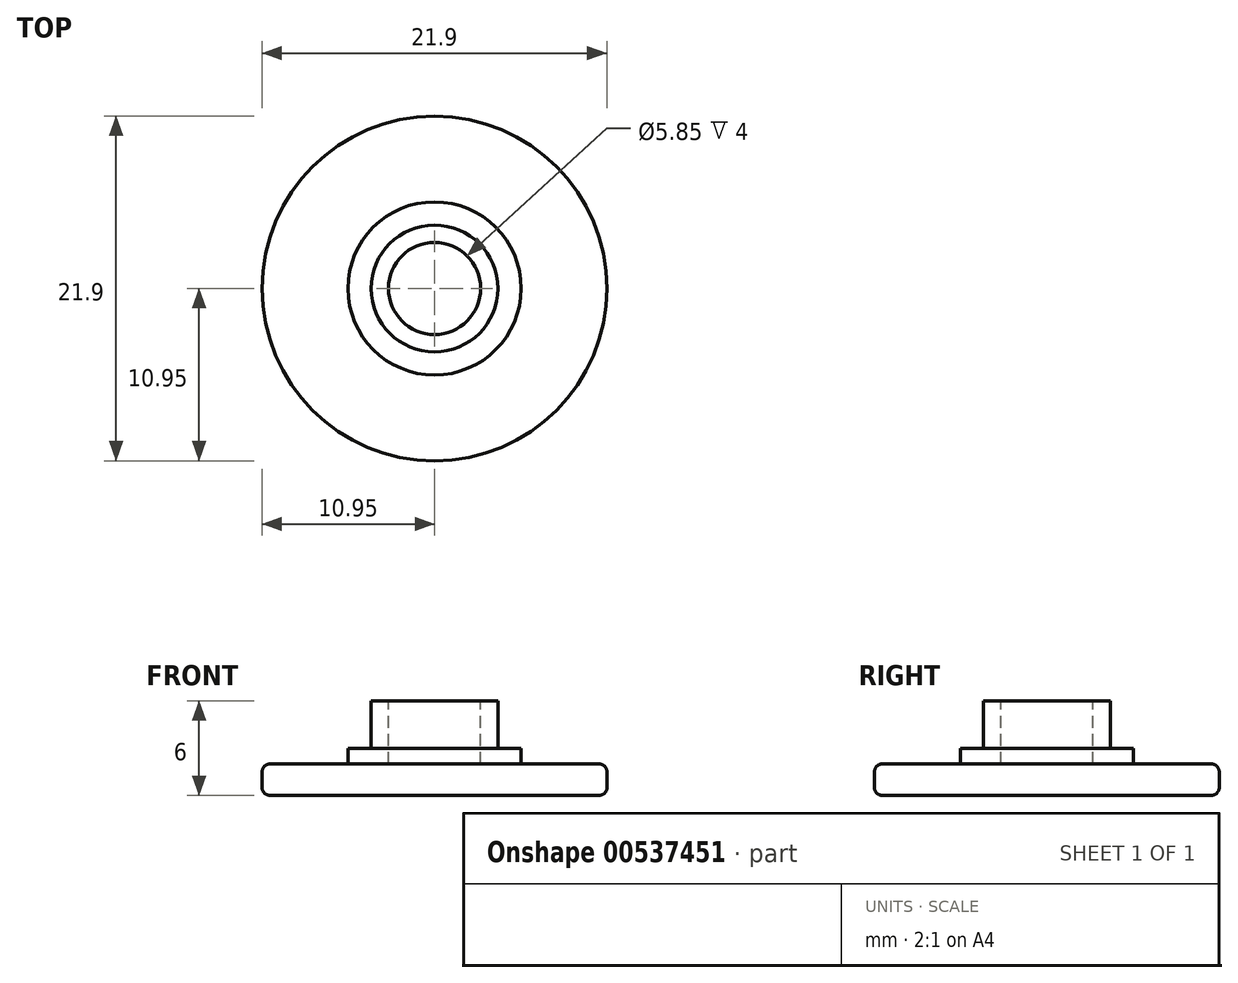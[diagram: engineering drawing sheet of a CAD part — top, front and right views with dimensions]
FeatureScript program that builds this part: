
annotation { "Feature Type Name" : "Feature", "Feature Type Description" : "" }
export const myFeature = defineFeature(function(context is Context, id is Id, definition is map)
    precondition{}
    {
        {
            var Q0;
            Q0=qCreatedBy(makeId("Top.planeOp"),FACE);
            var sketch = newSketch(context, id + "F0", { "sketchPlane" : qUnion([Q0])});
            skCircle(sketch, "E0", {"center": v(0, 0) * mm, "radius": 0.07 * mm});
            skCircle(sketch, "E1", {"center": v(0, 0) * mm, "radius": 10.95 * mm});
            skSolve(sketch);
        }
        {
            var Q0;
            Q0=qCreatedBy(makeId("Top.planeOp"),FACE);
            var sketch = newSketch(context, id + "F1", { "sketchPlane" : qUnion([Q0])});
            skCircle(sketch, "E2", {"center": v(0, 0) * mm, "radius": 5.5 * mm});
            skSolve(sketch);
        }
        {
            var Q0;
            Q0=qCreatedBy(makeId("Top.planeOp"),FACE);
            var sketch = newSketch(context, id + "F2", { "sketchPlane" : qUnion([Q0])});
            skCircle(sketch, "E3", {"center": v(0, 0) * mm, "radius": 4.03 * mm});
            skSolve(sketch);
        }
        {
            var Q0;
            Q0=qSketchRegion(id+"F0",true);
            extrude(context, id + "F3", {"entities" : qUnion([Q0]), "depth" : 2 * mm});
        }
        {
            var Q0;
            Q0=qSketchRegion(id+"F1",true);
            extrude(context, id + "F4", {"entities" : qUnion([Q0]), "operationType" : NewBodyOperationType.ADD, "depth" : 3 * mm});
        }
        {
            var Q0;
            Q0=qSketchRegion(id+"F2",true);
            extrude(context, id + "F5", {"entities" : qUnion([Q0]), "operationType" : NewBodyOperationType.ADD, "depth" : 6 * mm, "offsetDistance" : 25 * mm});
        }
        {
            var Q0;
            Q0=makeQuery(id+"F3.opExtrude","SWEPT_FACE",FACE,{"disambiguationData":[OSD([sQuery(id+"F0.wireOp",EDGE,"E1")])]});
            fillet(context, id + "F6", {"entities" : qUnion([Q0]), "radius" : .5 * mm, "tangentPropagation" : true, "allowEdgeOverflow" : false});
        }
        {
            var Q0;
            Q0=makeQuery(id+"F5.opExtrude","CAP_FACE",FACE,{"disambiguationData":[OSD([sQuery(id+"F2.wireOp",EDGE,"E3")])],"isStart":false});
            var sketch = newSketch(context, id + "F7", { "sketchPlane" : qUnion([Q0])});
            skCircle(sketch, "E4.0", {"center": v(0, 0) * mm, "radius": 2.92 * mm});
            skSolve(sketch);
        }
        {
            var Q0;
            Q0=qSketchRegion(id+"F7",true);
            extrude(context, id + "F8", {"entities" : qUnion([Q0]), "operationType" : NewBodyOperationType.REMOVE, "oppositeDirection" : true, "depth" : 4 * mm});
        }
    });
